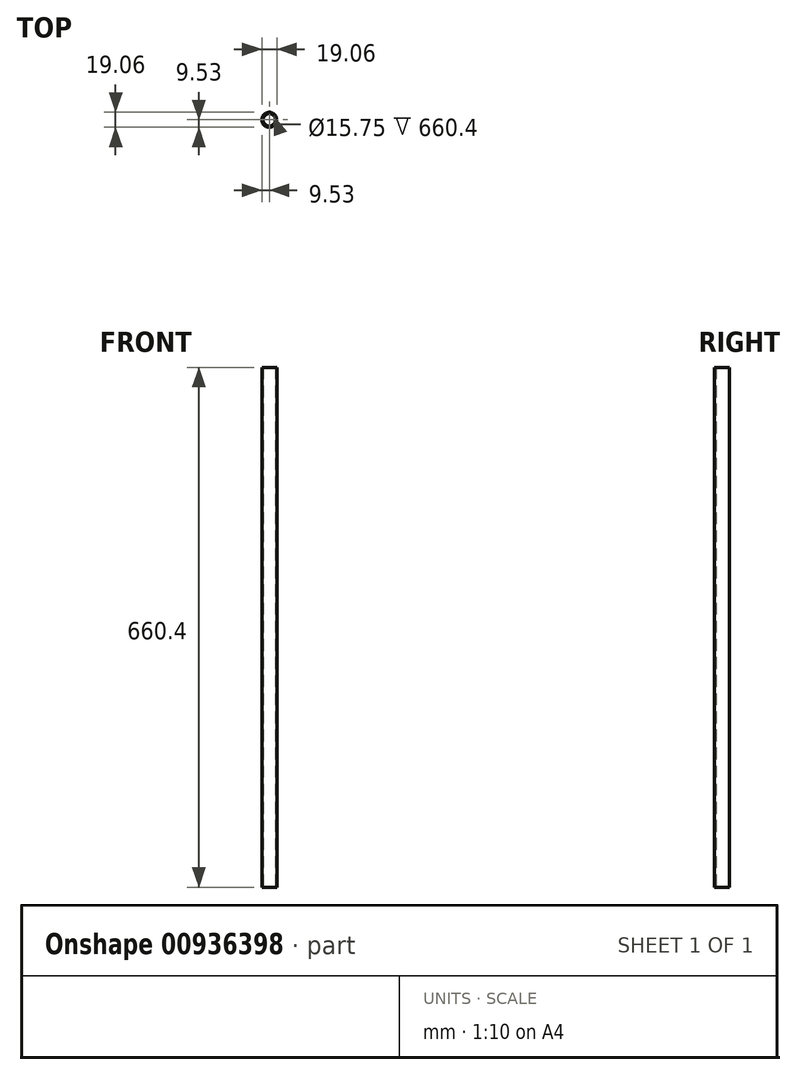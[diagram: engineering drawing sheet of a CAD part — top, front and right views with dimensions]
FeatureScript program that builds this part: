
annotation { "Feature Type Name" : "Feature", "Feature Type Description" : "" }
export const myFeature = defineFeature(function(context is Context, id is Id, definition is map)
    precondition{}
    {
        {
            var Q0;
            Q0=qCreatedBy(makeId("Top.planeOp"),FACE);
            var sketch = newSketch(context, id + "F0", { "sketchPlane" : qUnion([Q0])});
            skCircle(sketch, "E0", {"center": v(0, 0) * mm, "radius": 9.53 * mm});
            skCircle(sketch, "E1", {"center": v(0, 0) * mm, "radius": 7.87 * mm});
            skSolve(sketch);
        }
        {
            var Q0;
            Q0=makeQuery(id+"F0.imprint","IMPRINT",FACE,{"disambiguationData":[TD([[makeQuery(id+"F0.imprint","IMPRINT",EDGE,{"derivedFrom":sQuery(id+"F0.wireOp",EDGE,"E0")}),1.0]])]});
            extrude(context, id + "F1", {"entities" : qUnion([Q0]), "depth" : 660.4 * mm, "offsetDistance" : 25.4 * mm});
        }
    });
